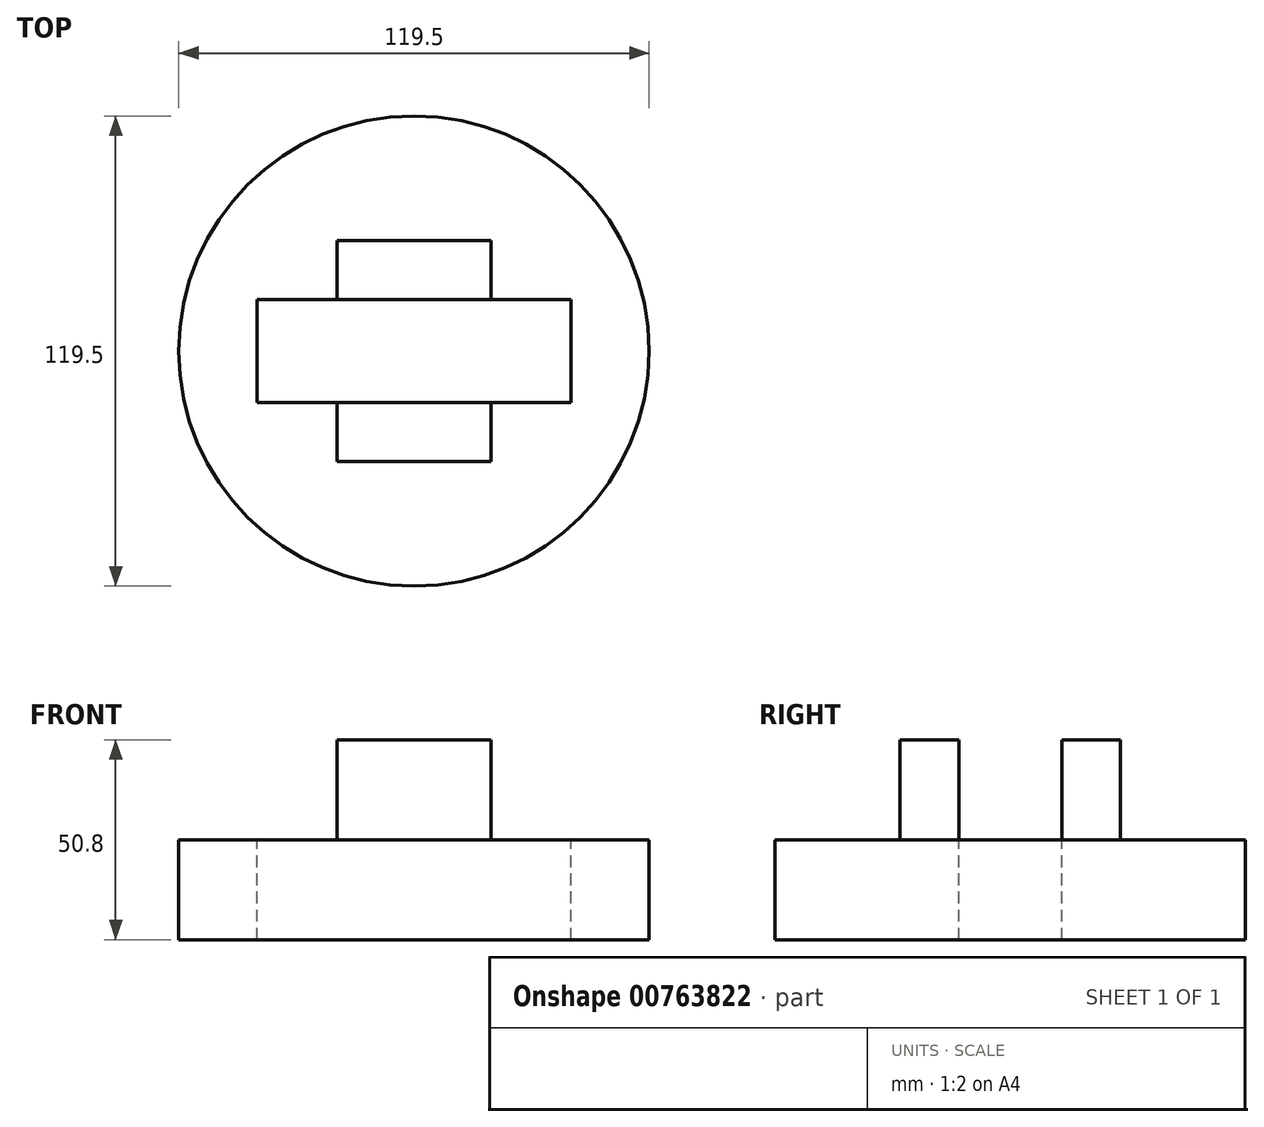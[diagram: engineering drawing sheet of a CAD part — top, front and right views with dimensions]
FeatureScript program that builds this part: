
annotation { "Feature Type Name" : "Feature", "Feature Type Description" : "" }
export const myFeature = defineFeature(function(context is Context, id is Id, definition is map)
    precondition{}
    {
        {
            var Q0;
            Q0=qCreatedBy(makeId("Top.planeOp"),FACE);
            var sketch = newSketch(context, id + "F0", { "sketchPlane" : qUnion([Q0])});
            skCircle(sketch, "E0", {"center": v(0, 0) * mm, "radius": 59.75 * mm});
            skSolve(sketch);
        }
        {
            var Q0;
            Q0=makeQuery(id+"F0.imprint","IMPRINT",FACE,{"disambiguationData":[TD([[makeQuery(id+"F0.imprint","IMPRINT",EDGE,{"derivedFrom":sQuery(id+"F0.wireOp",EDGE,"E0")}),1.0]])]});
            extrude(context, id + "F1", {"entities" : qUnion([Q0]), "depth" : 25.4 * mm, "offsetDistance" : 25.4 * mm});
        }
        {
            var Q0;
            Q0=makeQuery(id+"F1.opExtrude","CAP_FACE",FACE,{"disambiguationData":[OSD([sQuery(id+"F0.wireOp",EDGE,"E0")])],"isStart":false});
            var sketch = newSketch(context, id + "F2", { "sketchPlane" : qUnion([Q0])});
            skLineSegment(sketch, "E1.bottom", {"start": v(-19.52, 28.02) * mm, "end": v(19.52, 28.02) * mm});
            skLineSegment(sketch, "E1.top", {"start": v(-19.52, -28.02) * mm, "end": v(19.52, -28.02) * mm});
            skLineSegment(sketch, "E1.left", {"start": v(-19.52, 28.02) * mm, "end": v(-19.52, -28.02) * mm});
            skLineSegment(sketch, "E1.right", {"start": v(19.52, 28.02) * mm, "end": v(19.52, -28.02) * mm});
            skPoint(sketch, "E1.middle", {"position": v(0, 0) * mm});
            skSolve(sketch);
        }
        {
            var Q0;
            Q0=makeQuery(id+"F2.imprint","IMPRINT",FACE,{"disambiguationData":[TD([[makeQuery(id+"F2.imprint","IMPRINT",EDGE,{"derivedFrom":sQuery(id+"F2.wireOp",EDGE,"E1.bottom")}),-1.0]])]});
            extrude(context, id + "F3", {"entities" : qUnion([Q0]), "operationType" : NewBodyOperationType.ADD, "depth" : 25.4 * mm, "offsetDistance" : 25.4 * mm});
        }
        {
            var Q0;
            Q0=makeQuery(id+"F3.opExtrude","CAP_FACE",FACE,{"disambiguationData":[OSD([sQuery(id+"F2.wireOp",EDGE,"E1.bottom"),sQuery(id+"F2.wireOp",EDGE,"E1.top"),sQuery(id+"F2.wireOp",EDGE,"E1.left"),sQuery(id+"F2.wireOp",EDGE,"E1.right")])],"isStart":false});
            var sketch = newSketch(context, id + "F4", { "sketchPlane" : qUnion([Q0])});
            skLineSegment(sketch, "E2.bottom", {"start": v(-10.9, 13.08) * mm, "end": v(10.9, 13.08) * mm});
            skLineSegment(sketch, "E2.top", {"start": v(-10.9, -13.08) * mm, "end": v(10.9, -13.08) * mm});
            skLineSegment(sketch, "E2.left", {"start": v(-10.9, 13.08) * mm, "end": v(-10.9, -13.08) * mm});
            skLineSegment(sketch, "E2.right", {"start": v(10.9, 13.08) * mm, "end": v(10.9, -13.08) * mm});
            skPoint(sketch, "E2.middle", {"position": v(0, 0) * mm});
            skSolve(sketch);
        }
        {
            var Q0;
            Q0=makeQuery(id+"F4.imprint","IMPRINT",FACE,{"disambiguationData":[TD([[makeQuery(id+"F4.imprint","IMPRINT",EDGE,{"derivedFrom":sQuery(id+"F4.wireOp",EDGE,"E2.bottom")}),-1.0]])]});
            extrude(context, id + "F5", {"entities" : qUnion([Q0]), "operationType" : NewBodyOperationType.REMOVE, "endBound" : BoundingType.UP_TO_NEXT, "oppositeDirection" : true, "depth" : 25.4 * mm, "offsetDistance" : 25.4 * mm});
        }
        {
            var Q0;
            Q0=makeQuery(id+"F3.opExtrude","CAP_FACE",FACE,{"disambiguationData":[OSD([sQuery(id+"F2.wireOp",EDGE,"E1.bottom"),sQuery(id+"F2.wireOp",EDGE,"E1.top"),sQuery(id+"F2.wireOp",EDGE,"E1.left"),sQuery(id+"F2.wireOp",EDGE,"E1.right")])],"isStart":false});
            var sketch = newSketch(context, id + "F6", { "sketchPlane" : qUnion([Q0])});
            skLineSegment(sketch, "E3.bottom", {"start": v(-39.9, 13.08) * mm, "end": v(39.9, 13.08) * mm});
            skLineSegment(sketch, "E3.top", {"start": v(-39.9, -13.08) * mm, "end": v(39.9, -13.08) * mm});
            skLineSegment(sketch, "E3.left", {"start": v(-39.9, 13.08) * mm, "end": v(-39.9, -13.08) * mm});
            skLineSegment(sketch, "E3.right", {"start": v(39.9, 13.08) * mm, "end": v(39.9, -13.08) * mm});
            skPoint(sketch, "E3.middle", {"position": v(0, 0) * mm});
            skSolve(sketch);
        }
        {
            var Q0;
            Q0 = qSketchRegion(id + "F6", true);
            extrude(context, id + "F7", {"entities" : qUnion([Q0]), "operationType" : NewBodyOperationType.REMOVE, "endBound" : BoundingType.THROUGH_ALL, "oppositeDirection" : true, "depth" : 25.4 * mm, "offsetDistance" : 25.4 * mm});
        }
    });
